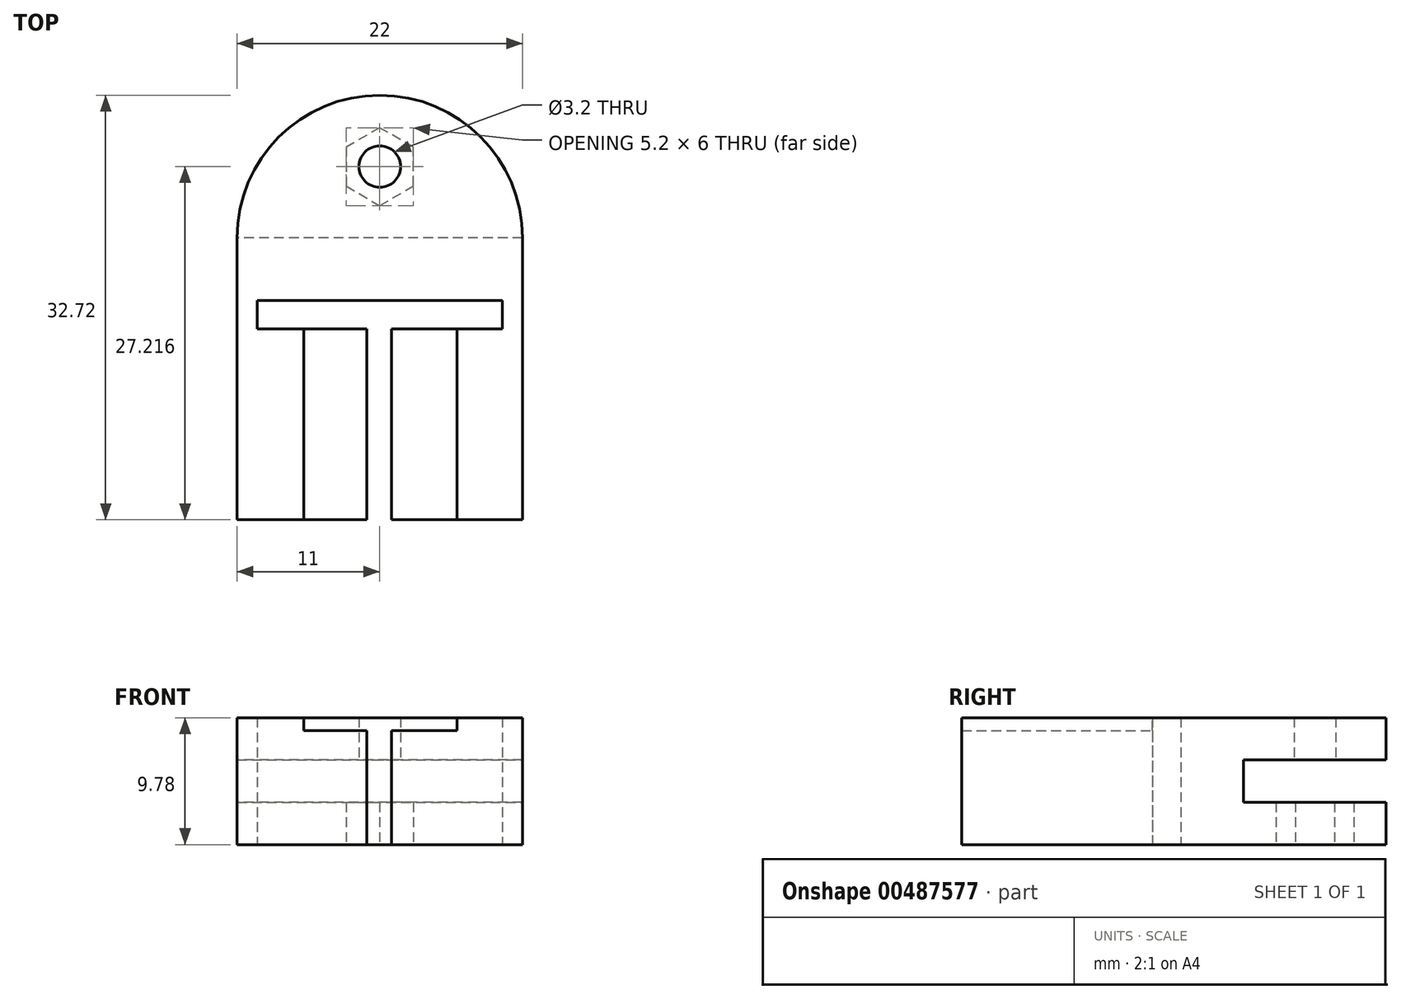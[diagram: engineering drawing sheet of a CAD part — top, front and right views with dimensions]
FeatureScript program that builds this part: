
annotation { "Feature Type Name" : "Feature", "Feature Type Description" : "" }
export const myFeature = defineFeature(function(context is Context, id is Id, definition is map)
    precondition{}
    {
        {
            var Q0;
            Q0=qCreatedBy(makeId("Top.planeOp"),FACE);
            var sketch = newSketch(context, id + "F0", { "sketchPlane" : qUnion([Q0])});
            skLineSegment(sketch, "E0.top", {"start": v(-33.41, 223.84) * mm, "end": v(-11.41, 223.84) * mm});
            skLineSegment(sketch, "E0.left", {"start": v(-33.41, 245.56) * mm, "end": v(-33.41, 223.84) * mm});
            skLineSegment(sketch, "E0.right", {"start": v(-11.41, 245.56) * mm, "end": v(-11.41, 223.84) * mm});
            skArc(sketch, "E1", {"start": v(-11.41, 245.56) * mm, "mid": v(-22.41, 256.56) * mm, "end": v(-33.41, 245.56) * mm});
            skCircle(sketch, "E2", {"center": v(-22.41, 251.06) * mm, "radius": 1.6 * mm});
            skLineSegment(sketch, "E3.bottom", {"start": v(-23.41, 223.84) * mm, "end": v(-21.51, 223.84) * mm});
            skLineSegment(sketch, "E3.top", {"start": v(-23.41, 240.74) * mm, "end": v(-21.51, 240.74) * mm});
            skLineSegment(sketch, "E3.left", {"start": v(-23.41, 223.84) * mm, "end": v(-23.41, 239.04) * mm});
            skLineSegment(sketch, "E3.right", {"start": v(-21.51, 223.84) * mm, "end": v(-21.51, 239.04) * mm});
            skLineSegment(sketch, "E4.bottom", {"start": v(-31.86, 240.74) * mm, "end": v(-12.96, 240.74) * mm});
            skLineSegment(sketch, "E4.top", {"start": v(-31.86, 239.04) * mm, "end": v(-23.41, 239.04) * mm});
            skLineSegment(sketch, "E4.left", {"start": v(-31.86, 240.74) * mm, "end": v(-31.86, 239.04) * mm});
            skLineSegment(sketch, "E4.right", {"start": v(-12.96, 240.74) * mm, "end": v(-12.96, 239.04) * mm});
            skLineSegment(sketch, "E5.trimOffspring", {"start": v(-21.51, 239.04) * mm, "end": v(-12.96, 239.04) * mm});
            skSolve(sketch);
        }
        {
            var Q0;
            {var subQ6=sQuery(id+"F0.wireOp",EDGE,"E0.left");Q0=makeQuery(id+"F0.imprint","IMPRINT",FACE,{"disambiguationData":[TD([[makeQuery(id+"F0.imprint","IMPRINT",EDGE,{"derivedFrom":subQ6}),1.0]])]});}
            extrude(context, id + "F1", {"entities" : qUnion([Q0]), "depth" : 9.78 * mm});
        }
        {
            var Q0;
            Q0=makeQuery(id+"F1.opExtrude","SWEPT_FACE",FACE,{"disambiguationData":[OSD([sQuery(id+"F0.wireOp",EDGE,"E0.left")])]});
            var sketch = newSketch(context, id + "F2", { "sketchPlane" : qUnion([Q0])});
            skLineSegment(sketch, "E6.bottom", {"start": v(-256.59, 6.53) * mm, "end": v(-245.56, 6.53) * mm});
            skLineSegment(sketch, "E6.top", {"start": v(-256.59, 3.25) * mm, "end": v(-245.56, 3.25) * mm});
            skLineSegment(sketch, "E6.left", {"start": v(-256.59, 6.53) * mm, "end": v(-256.59, 3.25) * mm});
            skLineSegment(sketch, "E6.right", {"start": v(-245.56, 6.53) * mm, "end": v(-245.56, 3.25) * mm});
            skSolve(sketch);
        }
        {
            var Q0;
            Q0=makeQuery(id+"F2.imprint","IMPRINT",FACE,{"disambiguationData":[TD([[makeQuery(id+"F2.imprint","IMPRINT",EDGE,{"derivedFrom":sQuery(id+"F2.wireOp",EDGE,"E6.bottom")}),-1.0]])]});
            extrude(context, id + "F3", {"entities" : qUnion([Q0]), "operationType" : NewBodyOperationType.REMOVE, "depth" : -22 * mm});
        }
        {
            var Q0;
            Q0=makeQuery(id+"F1.opExtrude","CAP_FACE",FACE,{"disambiguationData":[OSD([sQuery(id+"F0.wireOp",EDGE,"E0.top"),sQuery(id+"F0.wireOp",EDGE,"E0.left"),sQuery(id+"F0.wireOp",EDGE,"E0.right"),sQuery(id+"F0.wireOp",EDGE,"E1"),sQuery(id+"F0.wireOp",EDGE,"E2"),sQuery(id+"F0.wireOp",EDGE,"E3.left"),sQuery(id+"F0.wireOp",EDGE,"E3.right"),sQuery(id+"F0.wireOp",EDGE,"E4.bottom"),sQuery(id+"F0.wireOp",EDGE,"E4.top"),sQuery(id+"F0.wireOp",EDGE,"E4.left"),sQuery(id+"F0.wireOp",EDGE,"E4.right"),sQuery(id+"F0.wireOp",EDGE,"E5.trimOffspring")])],"isStart":false});
            var sketch = newSketch(context, id + "F4", { "sketchPlane" : qUnion([Q0])});
            skLineSegment(sketch, "E7.bottom", {"start": v(-28.27, 239.04) * mm, "end": v(-23.41, 239.04) * mm});
            skLineSegment(sketch, "E7.top", {"start": v(-28.27, 223.84) * mm, "end": v(-23.41, 223.84) * mm});
            skLineSegment(sketch, "E7.left", {"start": v(-28.27, 239.04) * mm, "end": v(-28.27, 223.84) * mm});
            skLineSegment(sketch, "E7.right", {"start": v(-23.41, 239.04) * mm, "end": v(-23.41, 223.84) * mm});
            skLineSegment(sketch, "E8.bottom", {"start": v(-21.51, 239.04) * mm, "end": v(-16.46, 239.04) * mm});
            skLineSegment(sketch, "E8.top", {"start": v(-21.51, 223.84) * mm, "end": v(-16.46, 223.84) * mm});
            skLineSegment(sketch, "E8.left", {"start": v(-21.51, 239.04) * mm, "end": v(-21.51, 223.84) * mm});
            skLineSegment(sketch, "E8.right", {"start": v(-16.46, 239.04) * mm, "end": v(-16.46, 223.84) * mm});
            skSolve(sketch);
        }
        {
            var Q0;
            Q0=makeQuery(id+"F4.imprint","IMPRINT",FACE,{"disambiguationData":[TD([[makeQuery(id+"F4.imprint","IMPRINT",EDGE,{"derivedFrom":sQuery(id+"F4.wireOp",EDGE,"E8.bottom")}),-1.0]])]});
            var Q1;
            Q1=makeQuery(id+"F4.imprint","IMPRINT",FACE,{"disambiguationData":[TD([[makeQuery(id+"F4.imprint","IMPRINT",EDGE,{"derivedFrom":sQuery(id+"F4.wireOp",EDGE,"E7.bottom")}),-1.0]])]});
            extrude(context, id + "F5", {"entities" : qUnion([Q0, Q1]), "operationType" : NewBodyOperationType.REMOVE, "oppositeDirection" : true, "depth" : 1 * mm, "offsetDistance" : 25 * mm});
        }
        {
            var Q0;
            Q0=makeQuery(id+"F3.boolean.opBoolean","COPY",FACE,{"derivedFrom":makeQuery(id+"F3.opExtrude","SWEPT_FACE",FACE,{"disambiguationData":[OSD([sQuery(id+"F2.wireOp",EDGE,"E6.top")])]})});
            var sketch = newSketch(context, id + "F6", { "sketchPlane" : qUnion([Q0])});
            skLineSegment(sketch, "E9.bottom", {"start": v(-33.41, 334.2) * mm, "end": v(-11.41, 334.2) * mm});
            skLineSegment(sketch, "E9.left", {"start": v(-33.41, 334.2) * mm, "end": v(-33.41, 290.2) * mm});
            skLineSegment(sketch, "E9.right", {"start": v(-11.41, 334.2) * mm, "end": v(-11.41, 290.2) * mm});
            skArc(sketch, "E10", {"start": v(-33.41, 290.2) * mm, "mid": v(-22.41, 279.2) * mm, "end": v(-11.41, 290.2) * mm});
            skCircle(sketch, "E11", {"center": v(-22.41, 284.6) * mm, "radius": 1.6 * mm});
            skSolve(sketch);
        }
        {
            var Q0;
            Q0=makeQuery(id+"F6.imprint","IMPRINT",FACE,{"disambiguationData":[TD([[makeQuery(id+"F6.imprint","IMPRINT",EDGE,{"derivedFrom":sQuery(id+"F6.wireOp",EDGE,"E9.bottom")}),-1.0]])]});
            extrude(context, id + "F7", {"entities" : qUnion([Q0]), "depth" : 3.26 * mm, "offsetDistance" : 25 * mm});
        }
        {
            var Q0;
            Q0=makeQuery(id+"F7.opExtrude","SWEPT_BODY",BODY,{"disambiguationData":[OSD([sQuery(id+"F6.wireOp",EDGE,"E9.bottom"),sQuery(id+"F6.wireOp",EDGE,"E9.left"),sQuery(id+"F6.wireOp",EDGE,"E9.right"),sQuery(id+"F6.wireOp",EDGE,"E10"),sQuery(id+"F6.wireOp",EDGE,"E11")])]});
            deleteBodies(context, id + "F8", {"entities" : qUnion([Q0])});
        }
        {
            var Q0;
            Q0=makeQuery(id+"F1.opExtrude","CAP_FACE",FACE,{"disambiguationData":[OSD([sQuery(id+"F0.wireOp",EDGE,"E0.top"),sQuery(id+"F0.wireOp",EDGE,"E0.left"),sQuery(id+"F0.wireOp",EDGE,"E0.right"),sQuery(id+"F0.wireOp",EDGE,"E1"),sQuery(id+"F0.wireOp",EDGE,"E2"),sQuery(id+"F0.wireOp",EDGE,"E3.left"),sQuery(id+"F0.wireOp",EDGE,"E3.right"),sQuery(id+"F0.wireOp",EDGE,"E4.bottom"),sQuery(id+"F0.wireOp",EDGE,"E4.top"),sQuery(id+"F0.wireOp",EDGE,"E4.left"),sQuery(id+"F0.wireOp",EDGE,"E4.right"),sQuery(id+"F0.wireOp",EDGE,"E5.trimOffspring")])],"isStart":true});
            var sketch = newSketch(context, id + "F9", { "sketchPlane" : qUnion([Q0])});
            skCircle(sketch, "E12.cCircle", {"center": v(-22.41, -251.06) * mm, "radius": 3 * mm, "construction": true});
            skLineSegment(sketch, "E12.0", {"start": v(-19.81, -252.56) * mm, "end": v(-22.41, -254.06) * mm});
            skLineSegment(sketch, "E12.1", {"start": v(-22.41, -254.06) * mm, "end": v(-25, -252.56) * mm});
            skLineSegment(sketch, "E12.2", {"start": v(-25, -252.56) * mm, "end": v(-25, -249.56) * mm});
            skLineSegment(sketch, "E12.3", {"start": v(-25, -249.56) * mm, "end": v(-22.41, -248.06) * mm});
            skLineSegment(sketch, "E12.4", {"start": v(-22.41, -248.06) * mm, "end": v(-19.81, -249.56) * mm});
            skLineSegment(sketch, "E12.5", {"start": v(-19.81, -249.56) * mm, "end": v(-19.81, -252.56) * mm});
            skSolve(sketch);
        }
        {
            var Q0;
            Q0=makeQuery(id+"F9.imprint","IMPRINT",FACE,{"disambiguationData":[TD([[makeQuery(id+"F9.imprint","IMPRINT",EDGE,{"derivedFrom":sQuery(id+"F9.wireOp",EDGE,"E12.0")}),-1.0]])]});
            extrude(context, id + "F10", {"entities" : qUnion([Q0]), "operationType" : NewBodyOperationType.REMOVE, "oppositeDirection" : true, "depth" : 3.26 * mm, "offsetDistance" : 25 * mm});
        }
        {
            var Q0;
            Q0=makeQuery(id+"F1.opExtrude","SWEPT_FACE",FACE,{"disambiguationData":[OSD([sQuery(id+"F0.wireOp",EDGE,"E4.top")])]});
            var Q1;
            Q1=makeQuery(id+"F1.opExtrude","SWEPT_FACE",FACE,{"disambiguationData":[OSD([sQuery(id+"F0.wireOp",EDGE,"E5.trimOffspring")])]});
            extrude(context, id + "F11", {"entities" : qUnion([Q0, Q1]), "operationType" : NewBodyOperationType.REMOVE, "oppositeDirection" : true, "depth" : 0.5 * mm, "offsetDistance" : 25 * mm});
        }
    });
